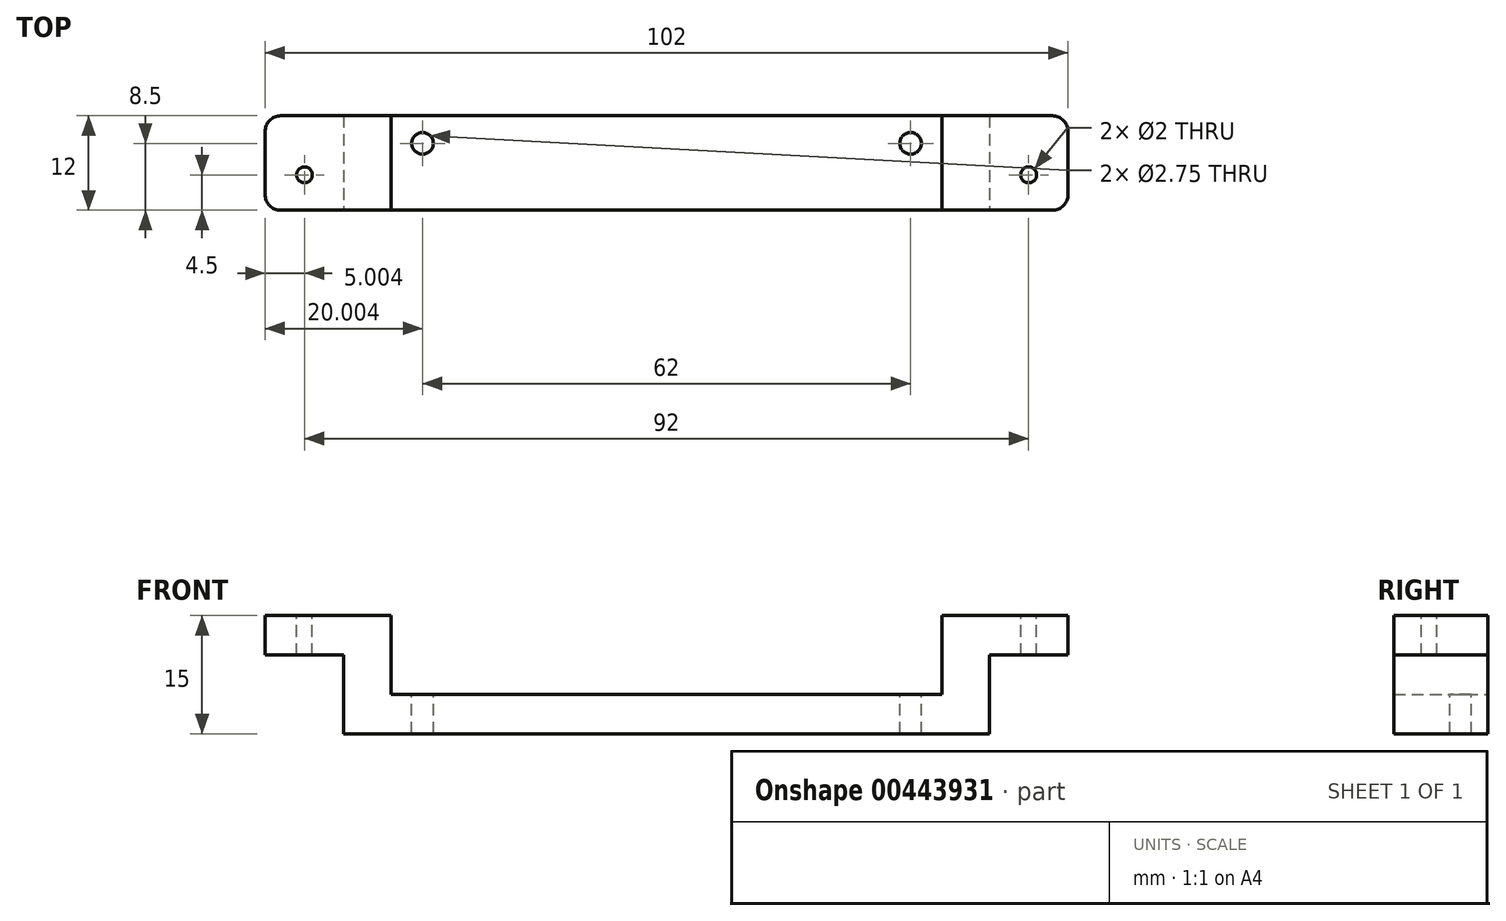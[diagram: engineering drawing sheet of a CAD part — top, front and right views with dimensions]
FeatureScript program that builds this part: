
annotation { "Feature Type Name" : "Feature", "Feature Type Description" : "" }
export const myFeature = defineFeature(function(context is Context, id is Id, definition is map)
    precondition{}
    {
        {
            var Q0;
            Q0=qCreatedBy(makeId("Top.planeOp"),FACE);
            var sketch = newSketch(context, id + "F0", { "sketchPlane" : qUnion([Q0])});
            skLineSegment(sketch, "E0.bottom", {"start": v(-13.49, 0) * mm, "end": v(84.51, 0) * mm});
            skLineSegment(sketch, "E0.top", {"start": v(-13.49, 12) * mm, "end": v(84.51, 12) * mm});
            skLineSegment(sketch, "E0.left", {"start": v(-15.49, 2) * mm, "end": v(-15.49, 10) * mm});
            skLineSegment(sketch, "E0.right", {"start": v(86.51, 2) * mm, "end": v(86.51, 10) * mm});
            skPoint(sketch, "E1.visualSharp", {"position": v(-15.49, 12) * mm});
            skArc(sketch, "E1.filletArc", {"start": v(-13.49, 12) * mm, "mid": v(-14.9, 11.41) * mm, "end": v(-15.49, 10) * mm});
            skPoint(sketch, "E2.visualSharp", {"position": v(-15.49, 0) * mm});
            skArc(sketch, "E2.filletArc", {"start": v(-15.49, 2) * mm, "mid": v(-14.9, 0.59) * mm, "end": v(-13.49, 0) * mm});
            skPoint(sketch, "E3.visualSharp", {"position": v(86.51, 12) * mm});
            skArc(sketch, "E3.filletArc", {"start": v(86.51, 10) * mm, "mid": v(85.93, 11.41) * mm, "end": v(84.51, 12) * mm});
            skPoint(sketch, "E4.visualSharp", {"position": v(86.51, 0) * mm});
            skArc(sketch, "E4.filletArc", {"start": v(84.51, 0) * mm, "mid": v(85.93, 0.59) * mm, "end": v(86.51, 2) * mm});
            skSolve(sketch);
        }
        {
            var Q0;
            Q0 = qSketchRegion(id + "F0", true);
            extrude(context, id + "F1", {"entities" : qUnion([Q0]), "depth" : 15 * mm});
        }
        {
            var Q0;
            Q0=makeQuery(id+"F1.opExtrude","CAP_FACE",FACE,{"disambiguationData":[OSD([sQuery(id+"F0.wireOp",EDGE,"E0.bottom"),sQuery(id+"F0.wireOp",EDGE,"E0.top"),sQuery(id+"F0.wireOp",EDGE,"E0.left"),sQuery(id+"F0.wireOp",EDGE,"E0.right"),sQuery(id+"F0.wireOp",EDGE,"E1.filletArc"),sQuery(id+"F0.wireOp",EDGE,"E2.filletArc"),sQuery(id+"F0.wireOp",EDGE,"E3.filletArc"),sQuery(id+"F0.wireOp",EDGE,"E4.filletArc")])],"isStart":false});
            var sketch = newSketch(context, id + "F2", { "sketchPlane" : qUnion([Q0])});
            skLineSegment(sketch, "E5.bottom", {"start": v(0.51, 0) * mm, "end": v(70.51, 0) * mm});
            skLineSegment(sketch, "E5.top", {"start": v(0.51, 12) * mm, "end": v(70.51, 12) * mm});
            skLineSegment(sketch, "E5.left", {"start": v(0.51, 0) * mm, "end": v(0.51, 12) * mm});
            skLineSegment(sketch, "E5.right", {"start": v(70.51, 0) * mm, "end": v(70.51, 12) * mm});
            skPoint(sketch, "E6.visualSharp", {"position": v(0.51, 12) * mm});
            skLineSegment(sketch, "E6.filletArc", {"start": v(0.51, 12) * mm, "end": v(0.51, 12) * mm});
            skPoint(sketch, "E7.visualSharp", {"position": v(0.51, 0) * mm});
            skLineSegment(sketch, "E7.filletArc", {"start": v(0.51, 0) * mm, "end": v(0.51, 0) * mm});
            skPoint(sketch, "E8.visualSharp", {"position": v(70.51, 0) * mm});
            skLineSegment(sketch, "E8.filletArc", {"start": v(70.51, 0) * mm, "end": v(70.51, 0) * mm});
            skPoint(sketch, "E9.visualSharp", {"position": v(70.51, 12) * mm});
            skLineSegment(sketch, "E9.filletArc", {"start": v(70.51, 12) * mm, "end": v(70.51, 12) * mm});
            skSolve(sketch);
        }
        {
            var Q0;
            Q0 = qSketchRegion(id + "F2", true);
            extrude(context, id + "F3", {"entities" : qUnion([Q0]), "operationType" : NewBodyOperationType.REMOVE, "oppositeDirection" : true, "depth" : 10 * mm});
        }
        {
            var Q0;
            Q0=makeQuery(id+"F3.boolean.opBoolean","COPY",FACE,{"derivedFrom":makeQuery(id+"F3.opExtrude","CAP_FACE",FACE,{"disambiguationData":[OSD([sQuery(id+"F2.wireOp",EDGE,"E5.bottom"),sQuery(id+"F2.wireOp",EDGE,"E5.top"),sQuery(id+"F2.wireOp",EDGE,"E5.left"),sQuery(id+"F2.wireOp",EDGE,"E5.right")])],"isStart":false})});
            var sketch = newSketch(context, id + "F4", { "sketchPlane" : qUnion([Q0])});
            skCircle(sketch, "E10", {"center": v(4.51, 8.5) * mm, "radius": 1.38 * mm});
            skCircle(sketch, "E11", {"center": v(66.51, 8.5) * mm, "radius": 1.38 * mm});
            skCircle(sketch, "E12", {"center": v(-10.49, 4.5) * mm, "radius": 1 * mm});
            skCircle(sketch, "E13", {"center": v(81.51, 4.5) * mm, "radius": 1 * mm});
            skSolve(sketch);
        }
        {
            var Q0;
            Q0 = qSketchRegion(id + "F4", true);
            extrude(context, id + "F5", {"entities" : qUnion([Q0]), "operationType" : NewBodyOperationType.REMOVE, "oppositeDirection" : true, "depth" : 25 * mm, "hasSecondDirection" : true, "secondDirectionOppositeDirection" : false, "secondDirectionDepth" : 25 * mm});
        }
        {
            var Q0;
            Q0=makeQuery(id+"F1.opExtrude","CAP_FACE",FACE,{"disambiguationData":[OSD([sQuery(id+"F0.wireOp",EDGE,"E0.bottom"),sQuery(id+"F0.wireOp",EDGE,"E0.top"),sQuery(id+"F0.wireOp",EDGE,"E0.left"),sQuery(id+"F0.wireOp",EDGE,"E0.right"),sQuery(id+"F0.wireOp",EDGE,"E1.filletArc"),sQuery(id+"F0.wireOp",EDGE,"E2.filletArc"),sQuery(id+"F0.wireOp",EDGE,"E3.filletArc"),sQuery(id+"F0.wireOp",EDGE,"E4.filletArc")])],"isStart":true});
            var sketch = newSketch(context, id + "F6", { "sketchPlane" : qUnion([Q0])});
            skLineSegment(sketch, "E14.bottom", {"start": v(-5.49, -12) * mm, "end": v(-15.58, -12) * mm});
            skLineSegment(sketch, "E14.top", {"start": v(-5.49, 0) * mm, "end": v(-15.58, 0) * mm});
            skLineSegment(sketch, "E14.left", {"start": v(-5.49, -12) * mm, "end": v(-5.49, 0) * mm});
            skLineSegment(sketch, "E14.right", {"start": v(-15.58, -12) * mm, "end": v(-15.58, 0) * mm});
            skLineSegment(sketch, "E15.bottom", {"start": v(76.51, -12) * mm, "end": v(86.64, -12) * mm});
            skLineSegment(sketch, "E15.top", {"start": v(76.51, 0) * mm, "end": v(86.64, 0) * mm});
            skLineSegment(sketch, "E15.left", {"start": v(76.51, -12) * mm, "end": v(76.51, 0) * mm});
            skLineSegment(sketch, "E15.right", {"start": v(86.64, -12) * mm, "end": v(86.64, 0) * mm});
            skSolve(sketch);
        }
        {
            var Q0;
            {var subQ1=sQuery(id+"F6.wireOp",EDGE,"E15.left");Q0=makeQuery(id+"F6.imprint","IMPRINT",FACE,{"disambiguationData":[TD([[makeQuery(id+"F6.imprint","IMPRINT",EDGE,{"derivedFrom":subQ1}),-1.0]])]});}
            var Q1;
            {var subQ1=sQuery(id+"F6.wireOp",EDGE,"E14.left");Q1=makeQuery(id+"F6.imprint","IMPRINT",FACE,{"disambiguationData":[TD([[makeQuery(id+"F6.imprint","IMPRINT",EDGE,{"derivedFrom":subQ1}),1.0]])]});}
            extrude(context, id + "F7", {"entities" : qUnion([Q0, Q1]), "operationType" : NewBodyOperationType.REMOVE, "oppositeDirection" : true, "depth" : 10 * mm});
        }
    });
